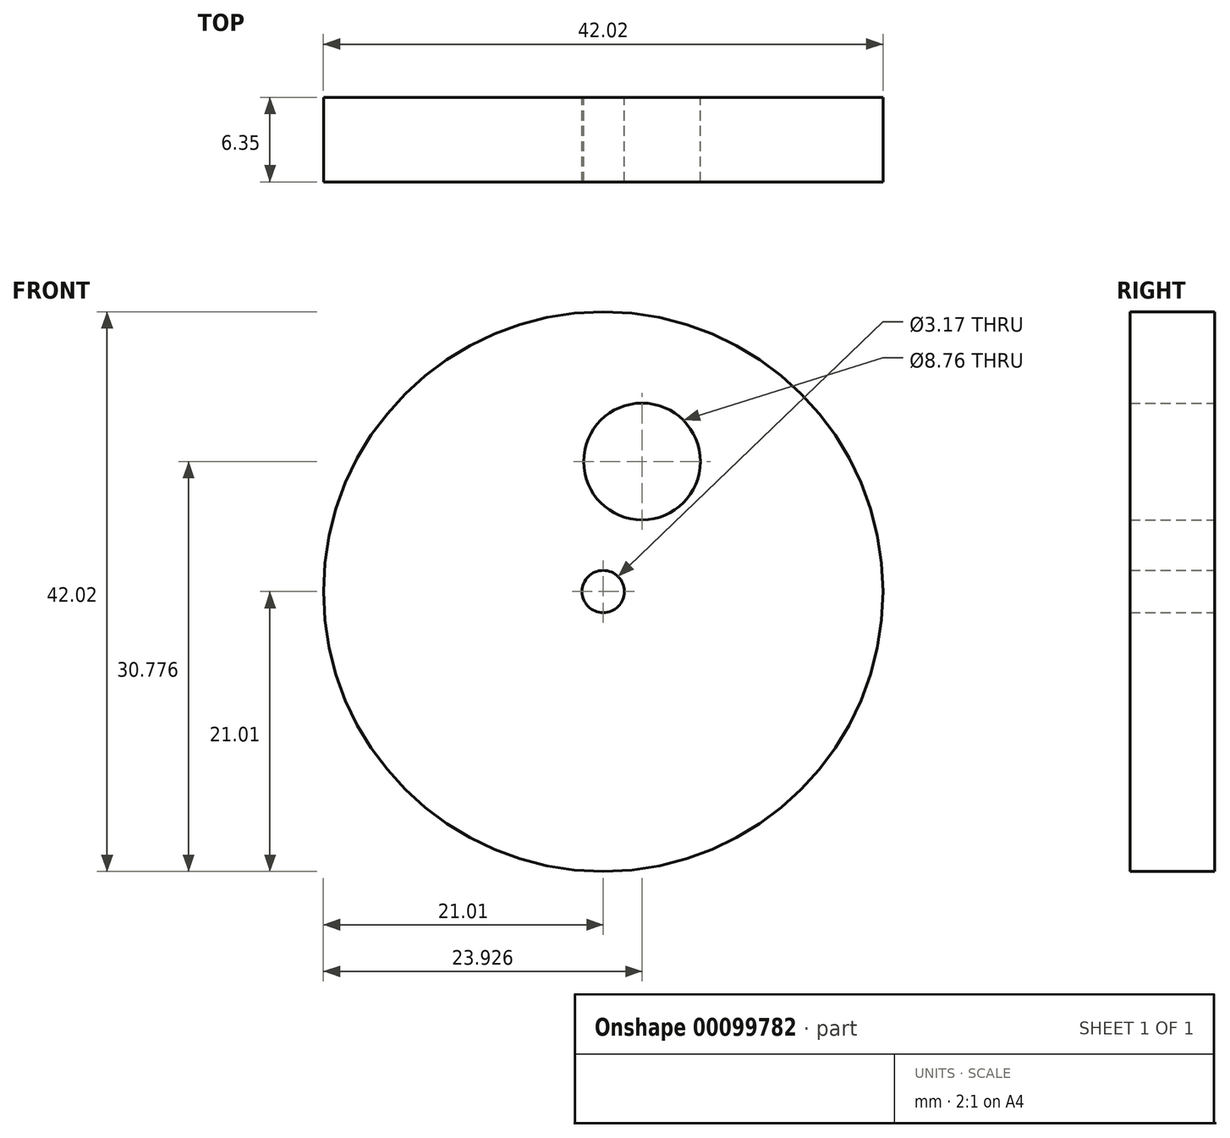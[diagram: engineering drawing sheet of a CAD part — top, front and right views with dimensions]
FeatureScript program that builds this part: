
annotation { "Feature Type Name" : "Feature", "Feature Type Description" : "" }
export const myFeature = defineFeature(function(context is Context, id is Id, definition is map)
    precondition{}
    {
        {
            var Q0;
            Q0=qCreatedBy(makeId("Front.planeOp"),FACE);
            var sketch = newSketch(context, id + "F0", { "sketchPlane" : qUnion([Q0])});
            skCircle(sketch, "E0", {"center": v(0, 0) * mm, "radius": 21 * mm});
            skCircle(sketch, "E1", {"center": v(0, 0) * mm, "radius": 1.59 * mm});
            skCircle(sketch, "E2", {"center": v(2.92, 9.77) * mm, "radius": 4.38 * mm});
            skSolve(sketch);
        }
        {
            var Q0;
            Q0=makeQuery(id+"F0.imprint","IMPRINT",FACE,{"disambiguationData":[TD([[makeQuery(id+"F0.imprint","IMPRINT",EDGE,{"derivedFrom":sQuery(id+"F0.wireOp",EDGE,"E0")}),1.0]])]});
            extrude(context, id + "F1", {"entities" : qUnion([Q0]), "depth" : 6.35 * mm});
        }
    });
